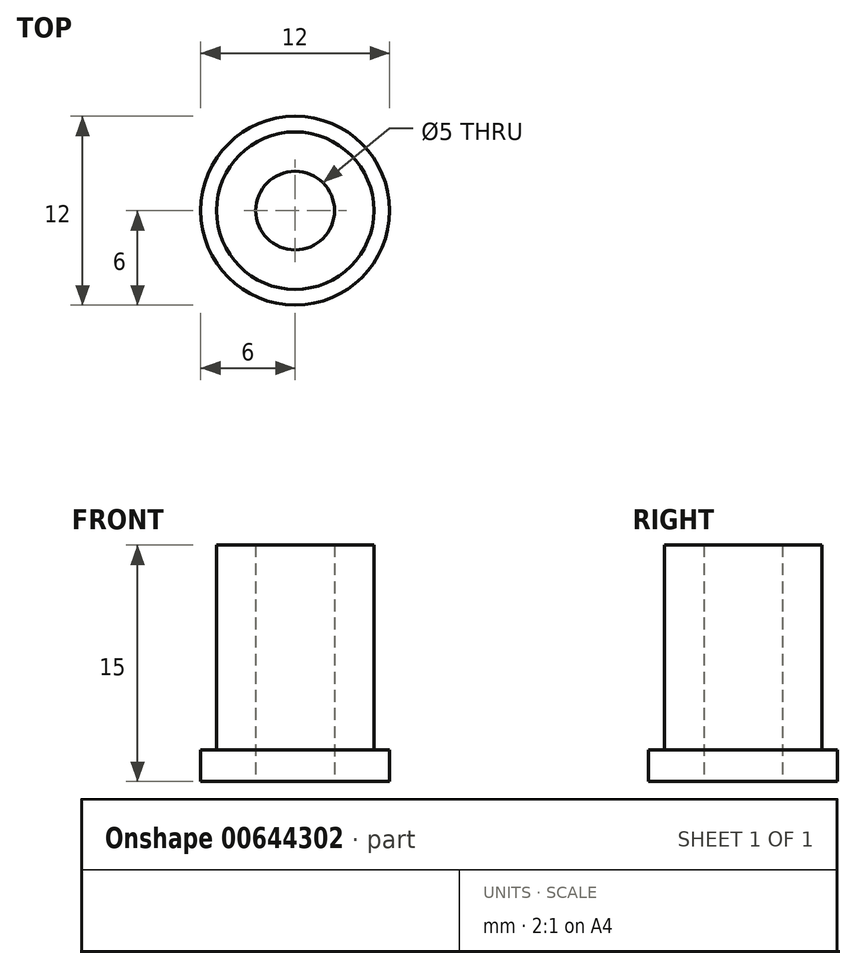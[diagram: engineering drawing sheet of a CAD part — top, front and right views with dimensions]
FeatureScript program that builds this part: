
annotation { "Feature Type Name" : "Feature", "Feature Type Description" : "" }
export const myFeature = defineFeature(function(context is Context, id is Id, definition is map)
    precondition{}
    {
        {
            var Q0;
            Q0=qCreatedBy(makeId("Top.planeOp"),FACE);
            var sketch = newSketch(context, id + "F0", { "sketchPlane" : qUnion([Q0])});
            skCircle(sketch, "E0", {"center": v(-122.73, 9.45) * mm, "radius": 10.27 * mm});
            skCircle(sketch, "E1", {"center": v(-122.73, 9.45) * mm, "radius": 5.06 * mm});
            skCircle(sketch, "E2", {"center": v(-122.73, 9.45) * mm, "radius": 16.45 * mm});
            skSolve(sketch);
        }
        {
            var Q0;
            Q0=qCreatedBy(makeId("Top.planeOp"),FACE);
            var sketch = newSketch(context, id + "F1", { "sketchPlane" : qUnion([Q0])});
            skCircle(sketch, "E3", {"center": v(0, 0) * mm, "radius": 5 * mm});
            skSolve(sketch);
        }
        {
            var Q0;
            Q0=qCreatedBy(makeId("Top.planeOp"),FACE);
            var sketch = newSketch(context, id + "F2", { "sketchPlane" : qUnion([Q0])});
            skCircle(sketch, "E4", {"center": v(0, 0) * mm, "radius": 2.5 * mm});
            skSolve(sketch);
        }
        {
            var Q0;
            Q0 = qSketchRegion(id + "F1", true);
            extrude(context, id + "F3", {"entities" : qUnion([Q0]), "depth" : 15 * mm, "offsetDistance" : 25 * mm});
        }
        {
            var Q0;
            Q0=qCreatedBy(makeId("Top.planeOp"),FACE);
            var sketch = newSketch(context, id + "F4", { "sketchPlane" : qUnion([Q0])});
            skCircle(sketch, "E5", {"center": v(0, 0) * mm, "radius": 6 * mm});
            skSolve(sketch);
        }
        {
            var Q0;
            Q0 = qSketchRegion(id + "F4", true);
            extrude(context, id + "F5", {"entities" : qUnion([Q0]), "operationType" : NewBodyOperationType.ADD, "depth" : 2 * mm, "offsetDistance" : 25 * mm});
        }
        {
            var Q0;
            Q0 = qSketchRegion(id + "F2", true);
            extrude(context, id + "F6", {"entities" : qUnion([Q0]), "operationType" : NewBodyOperationType.REMOVE, "depth" : 25 * mm, "offsetDistance" : 25 * mm});
        }
    });
